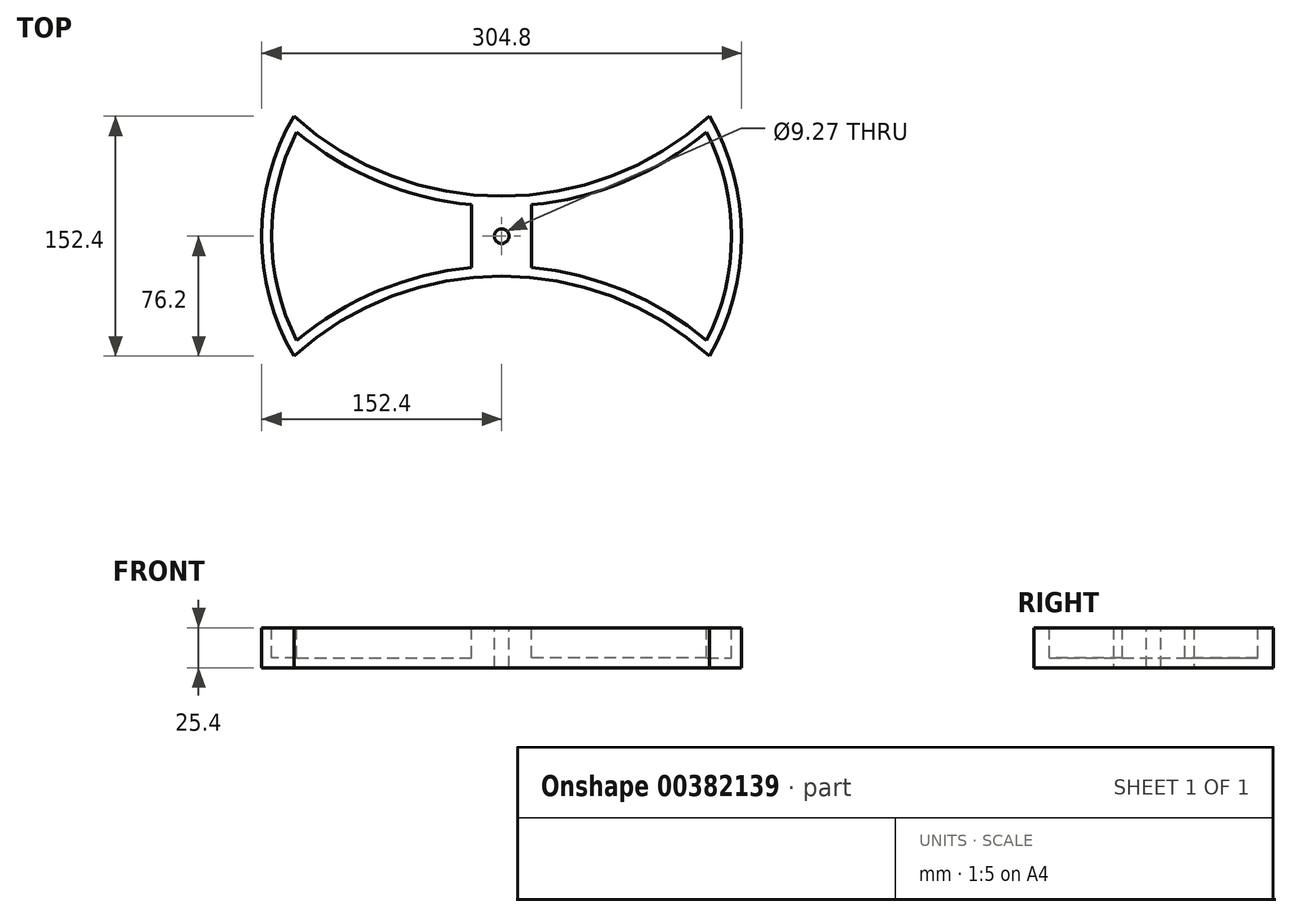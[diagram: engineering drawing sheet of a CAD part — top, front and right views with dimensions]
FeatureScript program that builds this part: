
annotation { "Feature Type Name" : "Feature", "Feature Type Description" : "" }
export const myFeature = defineFeature(function(context is Context, id is Id, definition is map)
    precondition{}
    {
        {
            var Q0;
            Q0=qCreatedBy(makeId("Top.planeOp"),FACE);
            var sketch = newSketch(context, id + "F0", { "sketchPlane" : qUnion([Q0])});
            skCircle(sketch, "E0", {"center": v(0, 0) * mm, "radius": 152.4 * mm});
            skLineSegment(sketch, "E1", {"start": v(0, 0) * mm, "end": v(0, 25.4) * mm});
            skLineSegment(sketch, "E2", {"start": v(0, 25.4) * mm, "end": v(0, 222.25) * mm});
            skCircle(sketch, "E3", {"center": v(0, 222.25) * mm, "radius": 196.85 * mm});
            skCircle(sketch, "E4.MirrorC", {"center": v(0, -222.25) * mm, "radius": 196.85 * mm});
            skSolve(sketch);
        }
        {
            var Q0;
            {var subQ0=sQuery(id+"F0.wireOp",EDGE,"E3");var subQ1=sQuery(id+"F0.wireOp",EDGE,"E0");var subQ2=makeQuery(id+"F0.imprint","INTERSECT",VERTEX,{"disambiguationData":[OD(0.0)],"derivedFrom":[subQ1,subQ0]});Q0=makeQuery(id+"F0.imprint","IMPRINT",FACE,{"disambiguationData":[TD([[makeQuery(id+"F0.imprint","IMPRINT",EDGE,{"disambiguationData":[TD([[subQ2,1.0]])],"derivedFrom":subQ1}),1.0]])]});}
            extrude(context, id + "F1", {"entities" : qUnion([Q0]), "depth" : 25.4 * mm});
        }
        {
            var Q0;
            Q0=makeQuery(id+"F1.opExtrude","CAP_FACE",FACE,{"disambiguationData":[OSD([sQuery(id+"F0.wireOp",EDGE,"E0"),sQuery(id+"F0.wireOp",EDGE,"E3"),sQuery(id+"F0.wireOp",EDGE,"E4.MirrorC")])],"isStart":false});
            var sketch = newSketch(context, id + "F2", { "sketchPlane" : qUnion([Q0])});
            skArc(sketch, "E5.0", {"start": v(-130.17, 66.22) * mm, "mid": v(-78.12, 34.67) * mm, "end": v(-19.05, 19.94) * mm});
            skArc(sketch, "E6.0", {"start": v(-130.17, -66.22) * mm, "mid": v(-78.12, -34.67) * mm, "end": v(-19.05, -19.94) * mm});
            skArc(sketch, "E7.0", {"start": v(130.17, -66.22) * mm, "mid": v(146.05, 0) * mm, "end": v(130.17, 66.22) * mm});
            skArc(sketch, "E8.0", {"start": v(-130.17, 66.22) * mm, "mid": v(-146.05, 0) * mm, "end": v(-130.17, -66.22) * mm});
            skLineSegment(sketch, "E9", {"start": v(-19.05, 0) * mm, "end": v(-19.05, 19.94) * mm});
            skLineSegment(sketch, "E10", {"start": v(-19.05, 0) * mm, "end": v(-19.05, -19.94) * mm});
            skLineSegment(sketch, "E11.MirrorCS", {"start": v(19.05, 0) * mm, "end": v(19.05, -19.94) * mm});
            skLineSegment(sketch, "E12.MirrorCS", {"start": v(19.05, 0) * mm, "end": v(19.05, 19.94) * mm});
            skArc(sketch, "E13.trimOffspring", {"start": v(19.05, 19.94) * mm, "mid": v(78.12, 34.67) * mm, "end": v(130.17, 66.22) * mm});
            skArc(sketch, "E14.trimOffspring", {"start": v(19.05, -19.94) * mm, "mid": v(78.12, -34.67) * mm, "end": v(130.17, -66.22) * mm});
            skSolve(sketch);
        }
        {
            var Q0;
            Q0=makeQuery(id+"F2.imprint","IMPRINT",FACE,{"disambiguationData":[TD([[makeQuery(id+"F2.imprint","IMPRINT",EDGE,{"derivedFrom":sQuery(id+"F2.wireOp",EDGE,"E5.0")}),-1.0]])]});
            var Q1;
            Q1=makeQuery(id+"F2.imprint","IMPRINT",FACE,{"disambiguationData":[TD([[makeQuery(id+"F2.imprint","IMPRINT",EDGE,{"derivedFrom":sQuery(id+"F2.wireOp",EDGE,"E7.0")}),1.0]])]});
            extrude(context, id + "F3", {"entities" : qUnion([Q0, Q1]), "operationType" : NewBodyOperationType.REMOVE, "oppositeDirection" : true, "depth" : 19.05 * mm});
        }
        {
            var Q0;
            Q0=makeQuery(id+"F1.opExtrude","CAP_FACE",FACE,{"disambiguationData":[OSD([sQuery(id+"F0.wireOp",EDGE,"E0"),sQuery(id+"F0.wireOp",EDGE,"E3"),sQuery(id+"F0.wireOp",EDGE,"E4.MirrorC")])],"isStart":false});
            var sketch = newSketch(context, id + "F4", { "sketchPlane" : qUnion([Q0])});
            skCircle(sketch, "E15", {"center": v(0, 0) * mm, "radius": 4.64 * mm});
            skSolve(sketch);
        }
        {
            var Q0;
            Q0 = qSketchRegion(id + "F4", true);
            extrude(context, id + "F5", {"entities" : qUnion([Q0]), "operationType" : NewBodyOperationType.REMOVE, "endBound" : BoundingType.UP_TO_NEXT, "oppositeDirection" : true, "depth" : 25.4 * mm});
        }
    });
